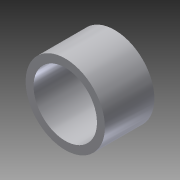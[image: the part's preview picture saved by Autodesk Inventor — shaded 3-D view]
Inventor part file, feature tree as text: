
AUTODESK INVENTOR PART (.ipt)
format: ipt  version: 2013 (Build 170138000, 138)  size: 84,480 bytes
history: native  units: in
note: dims shown in document units (in); Inventor stores cm internally (conversion verified against a paired STEP export)
features: extrude x1, sketch x1
ambient origin geometry x8: Origin, YZ Plane, XZ Plane, XY Plane, X Axis, Y Axis, Z Axis, Center Point
bodies: Solid1 (feature_tree)
feature tree (2):
  extrude  "Extrusion1"  Depth=0.5in
  sketch  "Sketch1"  dims[d0=0.625in d1=0.5in d2=0.39in d3=0.0in]
